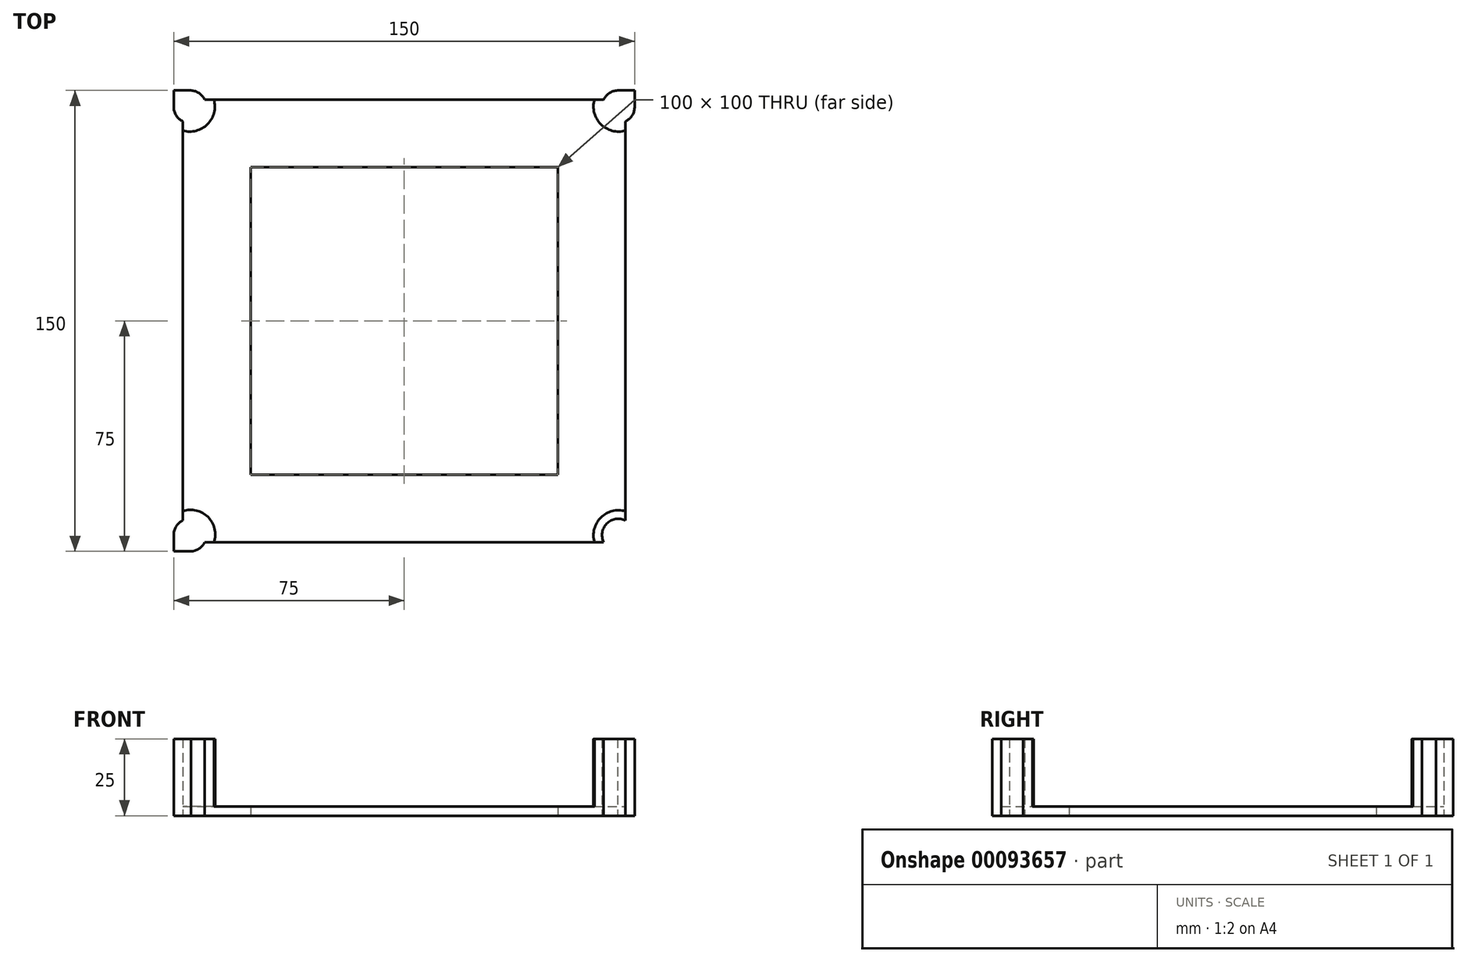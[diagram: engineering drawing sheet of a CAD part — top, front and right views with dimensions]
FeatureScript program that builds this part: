
annotation { "Feature Type Name" : "Feature", "Feature Type Description" : "" }
export const myFeature = defineFeature(function(context is Context, id is Id, definition is map)
    precondition{}
    {
        {
            var Q0;
            Q0=qCreatedBy(makeId("Top.planeOp"),FACE);
            var sketch = newSketch(context, id + "F0", { "sketchPlane" : qUnion([Q0])});
            skLineSegment(sketch, "E0.bottom", {"start": v(-75, 75) * mm, "end": v(75, 75) * mm});
            skLineSegment(sketch, "E0.top", {"start": v(-75, -75) * mm, "end": v(75, -75) * mm});
            skLineSegment(sketch, "E0.left", {"start": v(-75, 75) * mm, "end": v(-75, -75) * mm});
            skLineSegment(sketch, "E0.right", {"start": v(75, 75) * mm, "end": v(75, -75) * mm});
            skPoint(sketch, "E0.middle", {"position": v(0, 0) * mm});
            skLineSegment(sketch, "E1.bottom", {"start": v(-50, 50) * mm, "end": v(50, 50) * mm});
            skLineSegment(sketch, "E1.top", {"start": v(-50, -50) * mm, "end": v(50, -50) * mm});
            skLineSegment(sketch, "E1.left", {"start": v(-50, 50) * mm, "end": v(-50, -50) * mm});
            skLineSegment(sketch, "E1.right", {"start": v(50, 50) * mm, "end": v(50, -50) * mm});
            skArc(sketch, "E2", {"start": v(-75, 70) * mm, "mid": v(-65.94, 65.94) * mm, "end": v(-70, 75) * mm});
            skArc(sketch, "E3", {"start": v(75, -70) * mm, "mid": v(65.94, -65.94) * mm, "end": v(70, -75) * mm});
            skArc(sketch, "E4", {"start": v(-70, -75) * mm, "mid": v(-65.94, -65.94) * mm, "end": v(-75, -70) * mm});
            skLineSegment(sketch, "E5", {"start": v(-72, -64.91) * mm, "end": v(-72, 64.91) * mm});
            skLineSegment(sketch, "E6", {"start": v(-64.91, -72) * mm, "end": v(64.91, -72) * mm});
            skLineSegment(sketch, "E7", {"start": v(72, -64.91) * mm, "end": v(72, 64.91) * mm});
            skLineSegment(sketch, "E8", {"start": v(-64.91, 72) * mm, "end": v(64.91, 72) * mm});
            skArc(sketch, "E9", {"start": v(70, 75) * mm, "mid": v(65.94, 65.94) * mm, "end": v(75, 70) * mm});
            skArc(sketch, "E10", {"start": v(-61.91, -72) * mm, "mid": v(-63.82, -63.82) * mm, "end": v(-72, -61.91) * mm});
            skArc(sketch, "E11", {"start": v(72, -61.91) * mm, "mid": v(64, -64) * mm, "end": v(61.91, -72) * mm});
            skArc(sketch, "E12", {"start": v(61.91, 72) * mm, "mid": v(64, 64) * mm, "end": v(72, 61.91) * mm});
            skArc(sketch, "E13", {"start": v(-72, 61.91) * mm, "mid": v(-64, 64) * mm, "end": v(-61.91, 72) * mm});
            skSolve(sketch);
        }
        {
            var Q0;
            {var subQ4=sQuery(id+"F0.wireOp",EDGE,"E2");var subQ6=sQuery(id+"F0.wireOp",EDGE,"E0.left");var subQ7=makeQuery(id+"F0.imprint","INTERSECT",VERTEX,{"disambiguationData":[OD(1.0)],"derivedFrom":[subQ6,subQ4]});Q0=makeQuery(id+"F0.imprint","IMPRINT",FACE,{"disambiguationData":[TD([[makeQuery(id+"F0.imprint","IMPRINT",EDGE,{"disambiguationData":[TD([[subQ7,-1.0]])],"derivedFrom":subQ6}),1.0]])]});}
            var Q1;
            {var subQ5=sQuery(id+"F0.wireOp",EDGE,"E13");Q1=makeQuery(id+"F0.imprint","IMPRINT",FACE,{"disambiguationData":[TD([[makeQuery(id+"F0.imprint","IMPRINT",EDGE,{"derivedFrom":subQ5}),1.0]])]});}
            var Q2;
            {var subQ3=sQuery(id+"F0.wireOp",EDGE,"E2");var subQ5=sQuery(id+"F0.wireOp",EDGE,"E0.bottom");var subQ6=makeQuery(id+"F0.imprint","INTERSECT",VERTEX,{"disambiguationData":[OD(1.0)],"derivedFrom":[subQ5,subQ3]});Q2=makeQuery(id+"F0.imprint","IMPRINT",FACE,{"disambiguationData":[TD([[makeQuery(id+"F0.imprint","IMPRINT",EDGE,{"disambiguationData":[TD([[subQ6,-1.0]])],"derivedFrom":subQ5}),-1.0]])]});}
            var Q3;
            {var subQ3=sQuery(id+"F0.wireOp",EDGE,"E12");Q3=makeQuery(id+"F0.imprint","IMPRINT",FACE,{"disambiguationData":[TD([[makeQuery(id+"F0.imprint","IMPRINT",EDGE,{"derivedFrom":subQ3}),1.0]])]});}
            var Q4;
            {var subQ5=sQuery(id+"F0.wireOp",EDGE,"E0.right");var subQ7=sQuery(id+"F0.wireOp",EDGE,"E9");var subQ8=makeQuery(id+"F0.imprint","INTERSECT",VERTEX,{"disambiguationData":[OD(1.0)],"derivedFrom":[subQ5,subQ7]});Q4=makeQuery(id+"F0.imprint","IMPRINT",FACE,{"disambiguationData":[TD([[makeQuery(id+"F0.imprint","IMPRINT",EDGE,{"disambiguationData":[TD([[subQ8,-1.0]])],"derivedFrom":subQ5}),-1.0]])]});}
            var Q5;
            {var subQ5=sQuery(id+"F0.wireOp",EDGE,"E11");Q5=makeQuery(id+"F0.imprint","IMPRINT",FACE,{"disambiguationData":[TD([[makeQuery(id+"F0.imprint","IMPRINT",EDGE,{"derivedFrom":subQ5}),1.0]])]});}
            var Q6;
            {var subQ1=sQuery(id+"F0.wireOp",EDGE,"E4");var subQ4=sQuery(id+"F0.wireOp",EDGE,"E0.top");var subQ5=makeQuery(id+"F0.imprint","INTERSECT",VERTEX,{"disambiguationData":[OD(1.0)],"derivedFrom":[subQ4,subQ1]});Q6=makeQuery(id+"F0.imprint","IMPRINT",FACE,{"disambiguationData":[TD([[makeQuery(id+"F0.imprint","IMPRINT",EDGE,{"disambiguationData":[TD([[subQ5,-1.0]])],"derivedFrom":subQ4}),1.0]])]});}
            var Q7;
            {var subQ5=sQuery(id+"F0.wireOp",EDGE,"E10");Q7=makeQuery(id+"F0.imprint","IMPRINT",FACE,{"disambiguationData":[TD([[makeQuery(id+"F0.imprint","IMPRINT",EDGE,{"derivedFrom":subQ5}),1.0]])]});}
            extrude(context, id + "F1", {"entities" : qUnion([Q0, Q1, Q2, Q3, Q4, Q5, Q6, Q7]), "depth" : 25 * mm});
        }
        {
            var Q0;
            Q0=makeQuery(id+"F0.imprint","IMPRINT",FACE,{"disambiguationData":[TD([[makeQuery(id+"F0.imprint","IMPRINT",EDGE,{"derivedFrom":sQuery(id+"F0.wireOp",EDGE,"E1.bottom")}),1.0]])]});
            extrude(context, id + "F2", {"entities" : qUnion([Q0]), "operationType" : NewBodyOperationType.ADD, "depth" : 3 * mm});
        }
    });
